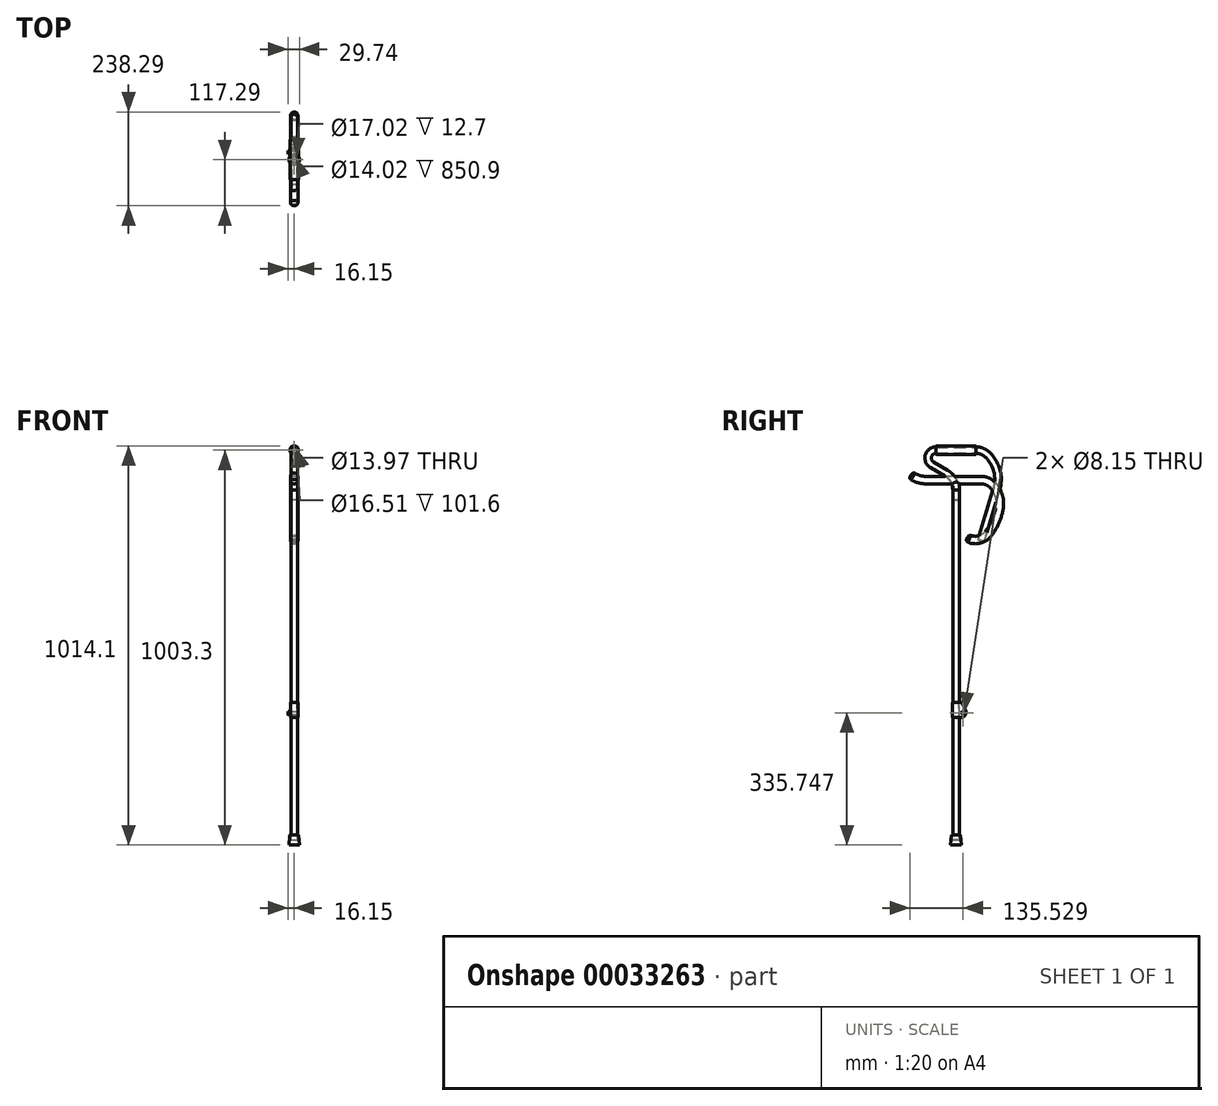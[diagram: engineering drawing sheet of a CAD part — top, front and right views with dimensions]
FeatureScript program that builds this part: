
annotation { "Feature Type Name" : "Feature", "Feature Type Description" : "" }
export const myFeature = defineFeature(function(context is Context, id is Id, definition is map)
    precondition{}
    {
        {
            var Q0;
            Q0=qCreatedBy(makeId("Top.planeOp"),FACE);
            var sketch = newSketch(context, id + "F0", { "sketchPlane" : qUnion([Q0])});
            skCircle(sketch, "E0", {"center": v(0, 0) * mm, "radius": 7.01 * mm});
            skCircle(sketch, "E1", {"center": v(0, 0) * mm, "radius": 8.26 * mm});
            skSolve(sketch);
        }
        {
            var Q0;
            Q0=qSketchRegion(id+"F0",true);
            extrude(context, id + "F1", {"entities" : qUnion([Q0]), "oppositeDirection" : true, "depth" : 889 * mm});
        }
        {
            var Q0;
            Q0=makeQuery(id+"F1.opExtrude","CAP_FACE",FACE,{"disambiguationData":[OSD([sQuery(id+"F0.wireOp",EDGE,"E0"),sQuery(id+"F0.wireOp",EDGE,"E1")])],"isStart":false});
            cPlane(context, id + "F2", {"entities" : qUnion([Q0]), "cplaneType" : CPlaneType.OFFSET, "offset" : 12.7 * mm, "oppositeDirection" : true, "width" : 152.4 * mm, "height" : 152.4 * mm});
        }
        {
            var Q0;
            Q0=qCreatedBy(id+"F2.planeOp",FACE);
            cPlane(context, id + "F3", {"entities" : qUnion([Q0]), "cplaneType" : CPlaneType.OFFSET, "offset" : 25.4 * mm, "width" : 152.4 * mm, "height" : 152.4 * mm});
        }
        {
            var Q0;
            Q0=qCreatedBy(id+"F2.planeOp",FACE);
            var sketch = newSketch(context, id + "F4", { "sketchPlane" : qUnion([Q0])});
            skCircle(sketch, "E2", {"center": v(0, 0) * mm, "radius": 8.5 * mm, "construction": true});
            skCircle(sketch, "E3", {"center": v(0, 0) * mm, "radius": 11.05 * mm});
            skSolve(sketch);
        }
        {
            var Q0;
            Q0=qCreatedBy(id+"F3.planeOp",FACE);
            var sketch = newSketch(context, id + "F5", { "sketchPlane" : qUnion([Q0])});
            skCircle(sketch, "E4", {"center": v(0, 0) * mm, "radius": 13.59 * mm});
            skSolve(sketch);
        }
        {
            var Q1;
            Q1=qSketchRegion(id+"F4",true);
            var Q2;
            Q2=qSketchRegion(id+"F5",true);
            loft(context, id + "F6", {"sheetProfilesArray" : [{ "sheetProfileEntities" : qUnion([Q1]) }, { "sheetProfileEntities" : qUnion([Q2]) }]});
        }
        {
            var Q0;
            Q0=makeQuery(id+"F4.imprint","IMPRINT",FACE,{"disambiguationData":[TD([[makeQuery(id+"F4.imprint","IMPRINT",EDGE,{"derivedFrom":sQuery(id+"F4.wireOp",EDGE,"E3")}),1.0]])]});
            var sketch = newSketch(context, id + "F7", { "sketchPlane" : qUnion([Q0])});
            skCircle(sketch, "E5", {"center": v(0, 0) * mm, "radius": 8.5 * mm});
            skSolve(sketch);
        }
        {
            var Q0;
            Q0=qSketchRegion(id+"F7",true);
            extrude(context, id + "F8", {"entities" : qUnion([Q0]), "operationType" : NewBodyOperationType.REMOVE, "depth" : 12.7 * mm});
        }
        {
            var Q0;
            Q0=qCreatedBy(makeId("Top.planeOp"),FACE);
            var sketch = newSketch(context, id + "F9", { "sketchPlane" : qUnion([Q0])});
            skCircle(sketch, "E6", {"center": v(0, 0) * mm, "radius": 8.26 * mm});
            skCircle(sketch, "E7", {"center": v(0, 0) * mm, "radius": 7.01 * mm});
            skSolve(sketch);
        }
        {
            var Q0;
            Q0=makeQuery(id+"F9.imprint","IMPRINT",FACE,{"disambiguationData":[TD([[makeQuery(id+"F9.imprint","IMPRINT",EDGE,{"derivedFrom":sQuery(id+"F9.wireOp",EDGE,"E7")}),1.0]])]});
            var Q1;
            Q1=sQuery(id+"F9.wireOp",EDGE,"E7");
            extrude(context, id + "F10", {"entities" : qUnion([Q0]), "surfaceEntities" : qUnion([Q1]), "oppositeDirection" : true, "depth" : 25.4 * mm});
        }
        {
            var Q0;
            Q0=makeQuery(id+"F9.imprint","IMPRINT",FACE,{"disambiguationData":[TD([[makeQuery(id+"F9.imprint","IMPRINT",EDGE,{"derivedFrom":sQuery(id+"F9.wireOp",EDGE,"E6")}),1.0]])]});
            var sketch = newSketch(context, id + "F11", { "sketchPlane" : qUnion([Q0])});
            skCircle(sketch, "E8", {"center": v(0, 0) * mm, "radius": 8.26 * mm});
            skSolve(sketch);
        }
        {
            var Q0;
            Q0=qSketchRegion(id+"F11",true);
            extrude(context, id + "F12", {"entities" : qUnion([Q0]), "operationType" : NewBodyOperationType.ADD, "depth" : 25.4 * mm});
        }
        {
            var Q0;
            Q0=qCreatedBy(makeId("Front.planeOp"),FACE);
            var sketch = newSketch(context, id + "F13", { "sketchPlane" : qUnion([Q0])});
            skCircle(sketch, "E9", {"center": v(0, 25.4) * mm, "radius": 9.53 * mm});
            skSolve(sketch);
        }
        {
            var Q0;
            Q0=qCreatedBy(makeId("Right.planeOp"),FACE);
            var sketch = newSketch(context, id + "F14", { "sketchPlane" : qUnion([Q0])});
            skLineSegment(sketch, "E10", {"start": v(0, 25.4) * mm, "end": v(-76.2, 25.4) * mm});
            skLineSegment(sketch, "E11", {"start": v(0, 25.4) * mm, "end": v(63.5, 25.4) * mm});
            skArc(sketch, "E12", {"start": v(63.5, 25.4) * mm, "mid": v(81.6, 21.26) * mm, "end": v(96.1, 9.67) * mm});
            skArc(sketch, "E13", {"start": v(-76.2, 25.4) * mm, "mid": v(-96.28, 28.66) * mm, "end": v(-114.3, 38.1) * mm});
            skArc(sketch, "E14", {"start": v(96.1, 9.67) * mm, "mid": v(109.4, -17.4) * mm, "end": v(110.23, -47.56) * mm});
            skArc(sketch, "E15", {"start": v(110.23, -47.56) * mm, "mid": v(99.8, -80.86) * mm, "end": v(81.96, -110.85) * mm});
            skArc(sketch, "E16", {"start": v(81.96, -110.85) * mm, "mid": v(57.3, -126.06) * mm, "end": v(28.77, -120.94) * mm});
            skSolve(sketch);
        }
        {
            var Q0;
            Q0=makeQuery(id+"F13.imprint","IMPRINT",FACE,{"disambiguationData":[TD([[makeQuery(id+"F13.imprint","IMPRINT",EDGE,{"derivedFrom":sQuery(id+"F13.wireOp",EDGE,"E9")}),1.0]])]});
            var Q1;
            Q1=sQuery(id+"F14.wireOp",EDGE,"E10");
            var Q2;
            Q2=sQuery(id+"F14.wireOp",EDGE,"E13");
            sweep(context, id + "F15", {"operationType" : NewBodyOperationType.ADD, "profiles" : qUnion([Q0]), "path" : qUnion([Q1, Q2])});
        }
        {
            var Q0;
            Q0=qSketchRegion(id+"F13",true);
            var Q1;
            Q1=sQuery(id+"F14.wireOp",EDGE,"E11");
            var Q2;
            Q2=sQuery(id+"F14.wireOp",EDGE,"E12");
            var Q3;
            Q3=sQuery(id+"F14.wireOp",EDGE,"E14");
            var Q4;
            Q4=sQuery(id+"F14.wireOp",EDGE,"E15");
            var Q5;
            Q5=sQuery(id+"F14.wireOp",EDGE,"E16");
            sweep(context, id + "F16", {"operationType" : NewBodyOperationType.ADD, "profiles" : qUnion([Q0]), "path" : qUnion([Q1, Q2, Q3, Q4, Q5])});
        }
        {
            var Q0;
            Q0=makeQuery(id+"F15.opSweep","CAP_EDGE",EDGE,{"disambiguationData":[OSD([sQuery(id+"F13.wireOp",EDGE,"E9"),sQuery(id+"F14.wireOp",VERTEX,"E13.end")])],"isStart":false});
            var Q1;
            Q1=makeQuery(id+"F16.opSweep","CAP_EDGE",EDGE,{"disambiguationData":[OSD([sQuery(id+"F13.wireOp",EDGE,"E9"),sQuery(id+"F14.wireOp",VERTEX,"E16.end")])],"isStart":false});
            fillet(context, id + "F17", {"entities" : qUnion([Q0, Q1]), "radius" : 6.35 * mm, "tangentPropagation" : true, "allowEdgeOverflow" : false});
        }
        {
            var Q0;
            Q0=qCreatedBy(makeId("Top.planeOp"),FACE);
            cPlane(context, id + "F18", {"entities" : qUnion([Q0]), "cplaneType" : CPlaneType.OFFSET, "offset" : 558.8 * mm, "oppositeDirection" : true, "width" : 152.4 * mm, "height" : 152.4 * mm});
        }
        {
            var Q0;
            Q0=qCreatedBy(id+"F18.planeOp",FACE);
            var sketch = newSketch(context, id + "F19", { "sketchPlane" : qUnion([Q0])});
            skArc(sketch, "E17", {"start": v(8.26, 0) * mm, "mid": v(0, -8.26) * mm, "end": v(-8.26, 0) * mm});
            skArc(sketch, "E18", {"start": v(9.25, 0) * mm, "mid": v(0, -9.25) * mm, "end": v(-9.25, 0) * mm});
            skLineSegment(sketch, "E19", {"start": v(-9.25, 0) * mm, "end": v(-9.25, 25.4) * mm});
            skLineSegment(sketch, "E20", {"start": v(-8.26, 0) * mm, "end": v(-8.26, 25.4) * mm});
            skLineSegment(sketch, "E21", {"start": v(-8.26, 25.4) * mm, "end": v(-9.25, 25.4) * mm});
            skLineSegment(sketch, "E22", {"start": v(8.26, 0) * mm, "end": v(8.26, 25.4) * mm});
            skLineSegment(sketch, "E23", {"start": v(8.26, 25.4) * mm, "end": v(9.25, 25.4) * mm});
            skLineSegment(sketch, "E24", {"start": v(9.25, 25.4) * mm, "end": v(9.25, 0) * mm});
            skSolve(sketch);
        }
        {
            var Q0;
            Q0 = qSketchRegion(id + "F19", true);
            extrude(context, id + "F20", {"entities" : qUnion([Q0]), "endBound" : BoundingType.SYMMETRIC, "depth" : 38.1 * mm});
        }
        {
            var Q0;
            Q0=makeQuery(id+"F20.opExtrude","SWEPT_FACE",FACE,{"disambiguationData":[OSD([sQuery(id+"F19.wireOp",EDGE,"E24")])]});
            var sketch = newSketch(context, id + "F21", { "sketchPlane" : qUnion([Q0])});
            skCircle(sketch, "E25", {"center": v(18.24, -565.95) * mm, "radius": 4.07 * mm});
            skLineSegment(sketch, "E26", {"start": v(14.95, -539.75) * mm, "end": v(25.4, -562.67) * mm});
            skLineSegment(sketch, "E27", {"start": v(14.95, -539.75) * mm, "end": v(25.4, -539.75) * mm});
            skLineSegment(sketch, "E28", {"start": v(25.4, -539.75) * mm, "end": v(25.4, -562.67) * mm});
            skSolve(sketch);
        }
        {
            var Q0;
            Q0 = qSketchRegion(id + "F21", true);
            extrude(context, id + "F22", {"entities" : qUnion([Q0]), "operationType" : NewBodyOperationType.REMOVE, "endBound" : BoundingType.THROUGH_ALL, "oppositeDirection" : true, "depth" : 25.4 * mm});
        }
        {
            var Q0;
            {var subQ0=sQuery(id+"F19.wireOp",EDGE,"E24");var subQ1=sQuery(id+"F19.wireOp",EDGE,"E22");var subQ2=sQuery(id+"F21.wireOp",EDGE,"E26");Q0=makeQuery(id+"F22.boolean.opBoolean","COPY",EDGE,{"disambiguationData":[TD([makeQuery(id+"F20.opExtrude","SWEPT_FACE",FACE,{"disambiguationData":[OSD([subQ1])]})])],"derivedFrom":makeQuery(id+"F22.opExtrude","SWEPT_EDGE",EDGE,{"disambiguationData":[OSD([subQ0,subQ2,sQuery(id+"F21.wireOp",EDGE,"E27")])]})});}
            var Q1;
            {var subQ0=sQuery(id+"F19.wireOp",EDGE,"E24");var subQ2=sQuery(id+"F19.wireOp",EDGE,"E19");var subQ3=sQuery(id+"F21.wireOp",EDGE,"E26");Q1=makeQuery(id+"F22.boolean.opBoolean","COPY",EDGE,{"disambiguationData":[TD([makeQuery(id+"F20.opExtrude","SWEPT_FACE",FACE,{"disambiguationData":[OSD([subQ2])]})])],"derivedFrom":makeQuery(id+"F22.opExtrude","SWEPT_EDGE",EDGE,{"disambiguationData":[OSD([subQ0,subQ3,sQuery(id+"F21.wireOp",EDGE,"E27")])]})});}
            var Q2;
            {var subQ0=sQuery(id+"F19.wireOp",EDGE,"E23");var subQ1=sQuery(id+"F19.wireOp",EDGE,"E24");var subQ2=sQuery(id+"F21.wireOp",EDGE,"E26");Q2=makeQuery(id+"F22.boolean.opBoolean","COPY",EDGE,{"disambiguationData":[TD([makeQuery(id+"F20.opExtrude","SWEPT_FACE",FACE,{"disambiguationData":[OSD([sQuery(id+"F19.wireOp",EDGE,"E22")])]})])],"derivedFrom":makeQuery(id+"F22.opExtrude","SWEPT_EDGE",EDGE,{"disambiguationData":[OSD([subQ0,subQ1,subQ2,sQuery(id+"F21.wireOp",EDGE,"E28")])]})});}
            var Q3;
            {var subQ0=sQuery(id+"F21.wireOp",EDGE,"E26");Q3=makeQuery(id+"F22.boolean.opBoolean","COPY",EDGE,{"disambiguationData":[TD([makeQuery(id+"F20.opExtrude","SWEPT_FACE",FACE,{"disambiguationData":[OSD([sQuery(id+"F19.wireOp",EDGE,"E19")])]})])],"derivedFrom":makeQuery(id+"F22.opExtrude","SWEPT_EDGE",EDGE,{"disambiguationData":[OSD([sQuery(id+"F19.wireOp",EDGE,"E23"),sQuery(id+"F19.wireOp",EDGE,"E24"),subQ0,sQuery(id+"F21.wireOp",EDGE,"E28")])]})});}
            var Q4;
            Q4=makeQuery(id+"F20.opExtrude","CAP_EDGE",EDGE,{"disambiguationData":[OSD([sQuery(id+"F19.wireOp",EDGE,"E23")])],"isStart":true});
            var Q5;
            Q5=makeQuery(id+"F20.opExtrude","CAP_EDGE",EDGE,{"disambiguationData":[OSD([sQuery(id+"F19.wireOp",EDGE,"E21")])],"isStart":true});
            fillet(context, id + "F23", {"entities" : qUnion([Q0, Q1, Q2, Q3, Q4, Q5]), "radius" : 12.7 * mm, "tangentPropagation" : true, "allowEdgeOverflow" : false});
        }
        {
            var Q0;
            Q0=makeQuery(id+"F20.opExtrude","SWEPT_FACE",FACE,{"disambiguationData":[OSD([sQuery(id+"F19.wireOp",EDGE,"E24")])]});
            var sketch = newSketch(context, id + "F24", { "sketchPlane" : qUnion([Q0])});
            skCircle(sketch, "E29", {"center": v(18.24, -565.95) * mm, "radius": 4.07 * mm});
            skSolve(sketch);
        }
        {
            var Q0;
            Q0 = qSketchRegion(id + "F24", true);
            extrude(context, id + "F25", {"entities" : qUnion([Q0]), "oppositeDirection" : true, "depth" : 25.4 * mm});
        }
        {
            var Q0;
            Q0=qCreatedBy(makeId("Right.planeOp"),FACE);
            var sketch = newSketch(context, id + "F26", { "sketchPlane" : qUnion([Q0])});
            skLineSegment(sketch, "E30", {"start": v(0, 0) * mm, "end": v(0, -52.8) * mm, "construction": true});
            skArc(sketch, "E31", {"start": v(0, 0) * mm, "mid": v(-6.5, 24.53) * mm, "end": v(-24.28, 42.64) * mm});
            skLineSegment(sketch, "E32", {"start": v(-24.28, 42.64) * mm, "end": v(-61, 64.45) * mm});
            skArc(sketch, "E33", {"start": v(-61, 64.45) * mm, "mid": v(-70.06, 86.91) * mm, "end": v(-50.8, 101.6) * mm});
            skLineSegment(sketch, "E34", {"start": v(-50.8, 101.6) * mm, "end": v(50.8, 101.6) * mm});
            skArc(sketch, "E35", {"start": v(50.8, 101.6) * mm, "mid": v(66.15, 98.7) * mm, "end": v(79.37, 90.37) * mm});
            skArc(sketch, "E36", {"start": v(79.37, 90.37) * mm, "mid": v(103.77, 49.95) * mm, "end": v(103.08, 2.74) * mm});
            skLineSegment(sketch, "E37", {"start": v(103.08, 2.74) * mm, "end": v(63.5, -128.16) * mm});
            skSolve(sketch);
        }
        {
            var Q0;
            Q0=qCreatedBy(makeId("Top.planeOp"),FACE);
            var sketch = newSketch(context, id + "F27", { "sketchPlane" : qUnion([Q0])});
            skCircle(sketch, "E38", {"center": v(0, 0) * mm, "radius": 8.26 * mm});
            skCircle(sketch, "E39", {"center": v(0, 0) * mm, "radius": 6.99 * mm});
            skSolve(sketch);
        }
        {
            var Q0;
            Q0 = qSketchRegion(id + "F27", true);
            var Q1;
            Q1 = qConstructionFilter(qBodyType(qCreatedBy(id + "F26" ,EDGE), BodyType.WIRE), ConstructionObject.NO);
            sweep(context, id + "F28", {"profiles" : qUnion([Q0]), "path" : qUnion([Q1])});
        }
        {
            var Q0;
            Q0=qCreatedBy(makeId("Front.planeOp"),FACE);
            var sketch = newSketch(context, id + "F29", { "sketchPlane" : qUnion([Q0])});
            skCircle(sketch, "E40", {"center": v(0, 101.6) * mm, "radius": 8.26 * mm});
            skCircle(sketch, "E41", {"center": v(0, 101.6) * mm, "radius": 10.8 * mm});
            skSolve(sketch);
        }
        {
            var Q0;
            Q0 = qSketchRegion(id + "F29", true);
            extrude(context, id + "F30", {"entities" : qUnion([Q0]), "endBound" : BoundingType.SYMMETRIC, "depth" : 101.6 * mm});
        }
        {
            var Q0;
            Q0=makeQuery(id+"F30.opExtrude","CAP_EDGE",EDGE,{"disambiguationData":[OSD([sQuery(id+"F29.wireOp",EDGE,"E41")])],"isStart":false});
            var Q1;
            Q1=makeQuery(id+"F30.opExtrude","CAP_EDGE",EDGE,{"disambiguationData":[OSD([sQuery(id+"F29.wireOp",EDGE,"E41")])],"isStart":true});
            fillet(context, id + "F31", {"entities" : qUnion([Q0, Q1]), "radius" : 1.27 * mm, "tangentPropagation" : true, "allowEdgeOverflow" : false});
        }
    });
